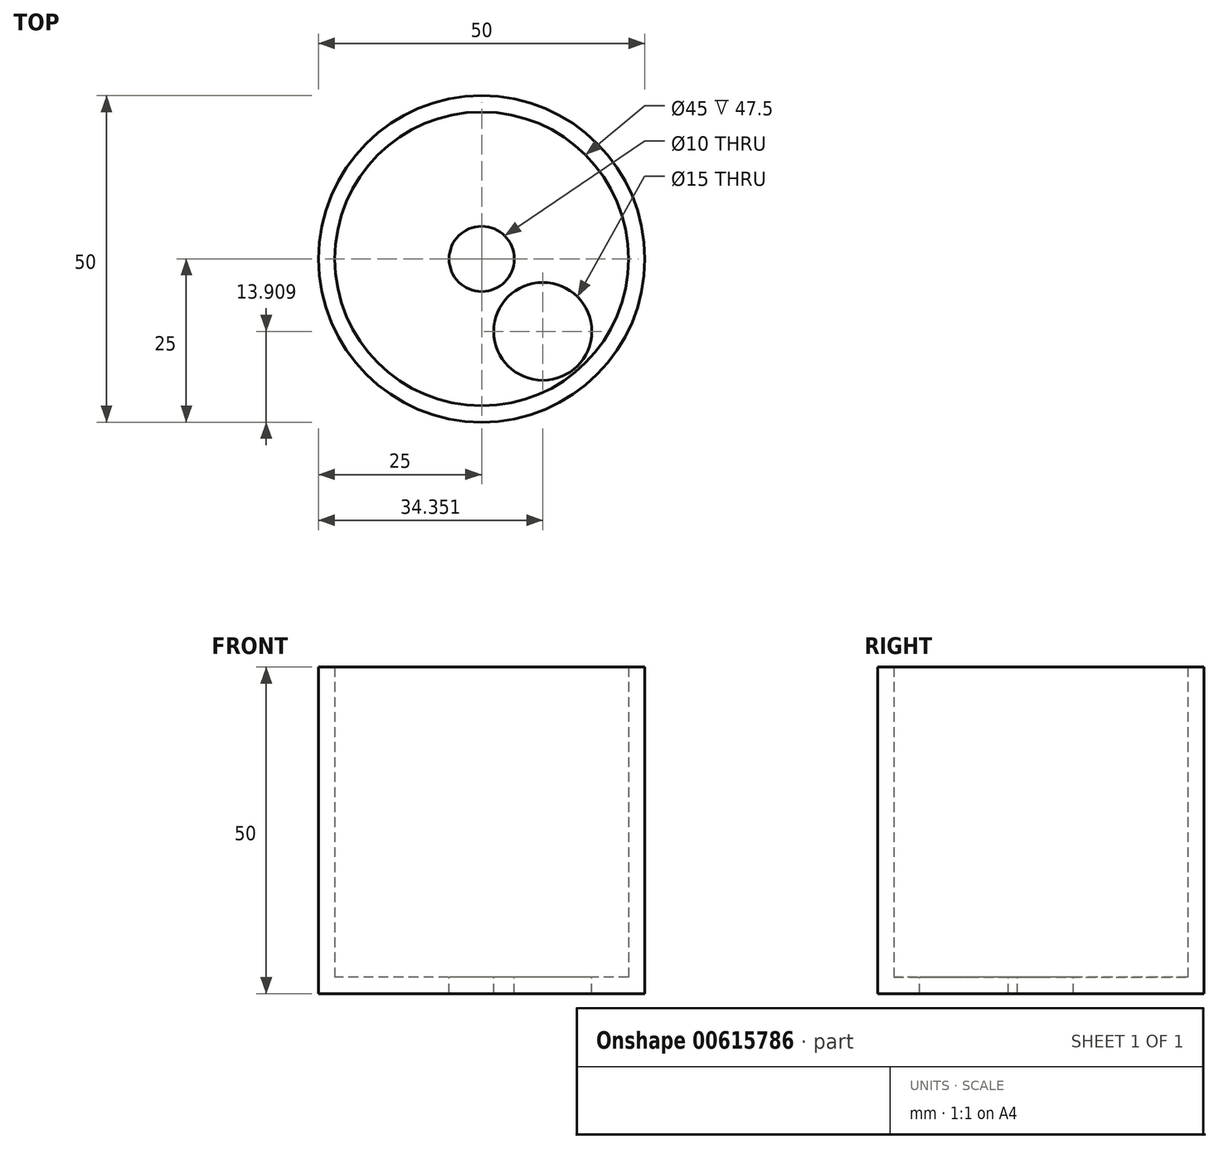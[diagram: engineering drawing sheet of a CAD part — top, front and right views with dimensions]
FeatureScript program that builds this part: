
annotation { "Feature Type Name" : "Feature", "Feature Type Description" : "" }
export const myFeature = defineFeature(function(context is Context, id is Id, definition is map)
    precondition{}
    {
        {
            var Q0;
            Q0=qCreatedBy(makeId("Top.planeOp"),FACE);
            var sketch = newSketch(context, id + "F0", { "sketchPlane" : qUnion([Q0])});
            skCircle(sketch, "E0", {"center": v(0, 0) * mm, "radius": 25 * mm});
            skSolve(sketch);
        }
        {
            var Q0;
            Q0=makeQuery(id+"F0.imprint","IMPRINT",FACE,{"disambiguationData":[TD([[makeQuery(id+"F0.imprint","IMPRINT",EDGE,{"derivedFrom":sQuery(id+"F0.wireOp",EDGE,"E0")}),1.0]])]});
            extrude(context, id + "F1", {"entities" : qUnion([Q0]), "depth" : (50) * mm, "offsetDistance" : 25 * mm});
        }
        {
            var Q0;
            Q0=makeQuery(id+"F1.opExtrude","CAP_FACE",FACE,{"disambiguationData":[OSD([sQuery(id+"F0.wireOp",EDGE,"E0")])],"isStart":false});
            shell(context, id + "F2", {"entities" : qUnion([Q0]), "thickness" : 2.5 * mm});
        }
        {
            var Q0;
            {var subQ0=sQuery(id+"F0.wireOp",EDGE,"E0");Q0=makeQuery(id+"F2.opShell","OFFSET_FACE",FACE,{"disambiguationData":[OSD([subQ0]),TDD([makeQuery(id+"F1.opExtrude","CAP_FACE",FACE,{"disambiguationData":[OSD([subQ0])],"isStart":true})])]});}
            var sketch = newSketch(context, id + "F3", { "sketchPlane" : qUnion([Q0])});
            skPoint(sketch, "E1", {"position": v(0, 0) * mm});
            skPoint(sketch, "E2", {"position": v(9.2, -11.53) * mm});
            skSolve(sketch);
        }
        {
            var Q0;
            Q0=sQuery(id+"F3.wireOp",VERTEX,"E1");
            var Q1;
            Q1=makeQuery(id+"F1.opExtrude","SWEPT_BODY",BODY,{"disambiguationData":[OSD([sQuery(id+"F0.wireOp",EDGE,"E0")])]});
            hole(context, id + "F4", {"style" : HoleStyle.SIMPLE, "endStyle" : HoleEndStyle.THROUGH, "holeDiameter" : 10 * mm, "majorDiameter" : 5 * mm, "isTappedThrough" : true, "tappedDepth" : 12 * mm, "tapClearance" : 3, "locations" : qUnion([Q0]), "scope" : qUnion([Q1])});
        }
        {
            var Q0;
            {var subQ0=sQuery(id+"F0.wireOp",EDGE,"E0");Q0=makeQuery(id+"F2.opShell","OFFSET_FACE",FACE,{"disambiguationData":[OSD([subQ0]),TDD([makeQuery(id+"F1.opExtrude","CAP_FACE",FACE,{"disambiguationData":[OSD([subQ0])],"isStart":true})])]});}
            var sketch = newSketch(context, id + "F5", { "sketchPlane" : qUnion([Q0])});
            skPoint(sketch, "E3", {"position": v(9.35, -11.1) * mm});
            skSolve(sketch);
        }
        {
            var Q0;
            Q0=sQuery(id+"F5.wireOp",VERTEX,"E3");
            var Q1;
            Q1=makeQuery(id+"F1.opExtrude","SWEPT_BODY",BODY,{"disambiguationData":[OSD([sQuery(id+"F0.wireOp",EDGE,"E0")])]});
            hole(context, id + "F6", {"style" : HoleStyle.SIMPLE, "endStyle" : HoleEndStyle.THROUGH, "holeDiameter" : 15 * mm, "majorDiameter" : 5 * mm, "isTappedThrough" : true, "tappedDepth" : 12 * mm, "tapClearance" : 3, "locations" : qUnion([Q0]), "scope" : qUnion([Q1])});
        }
    });
